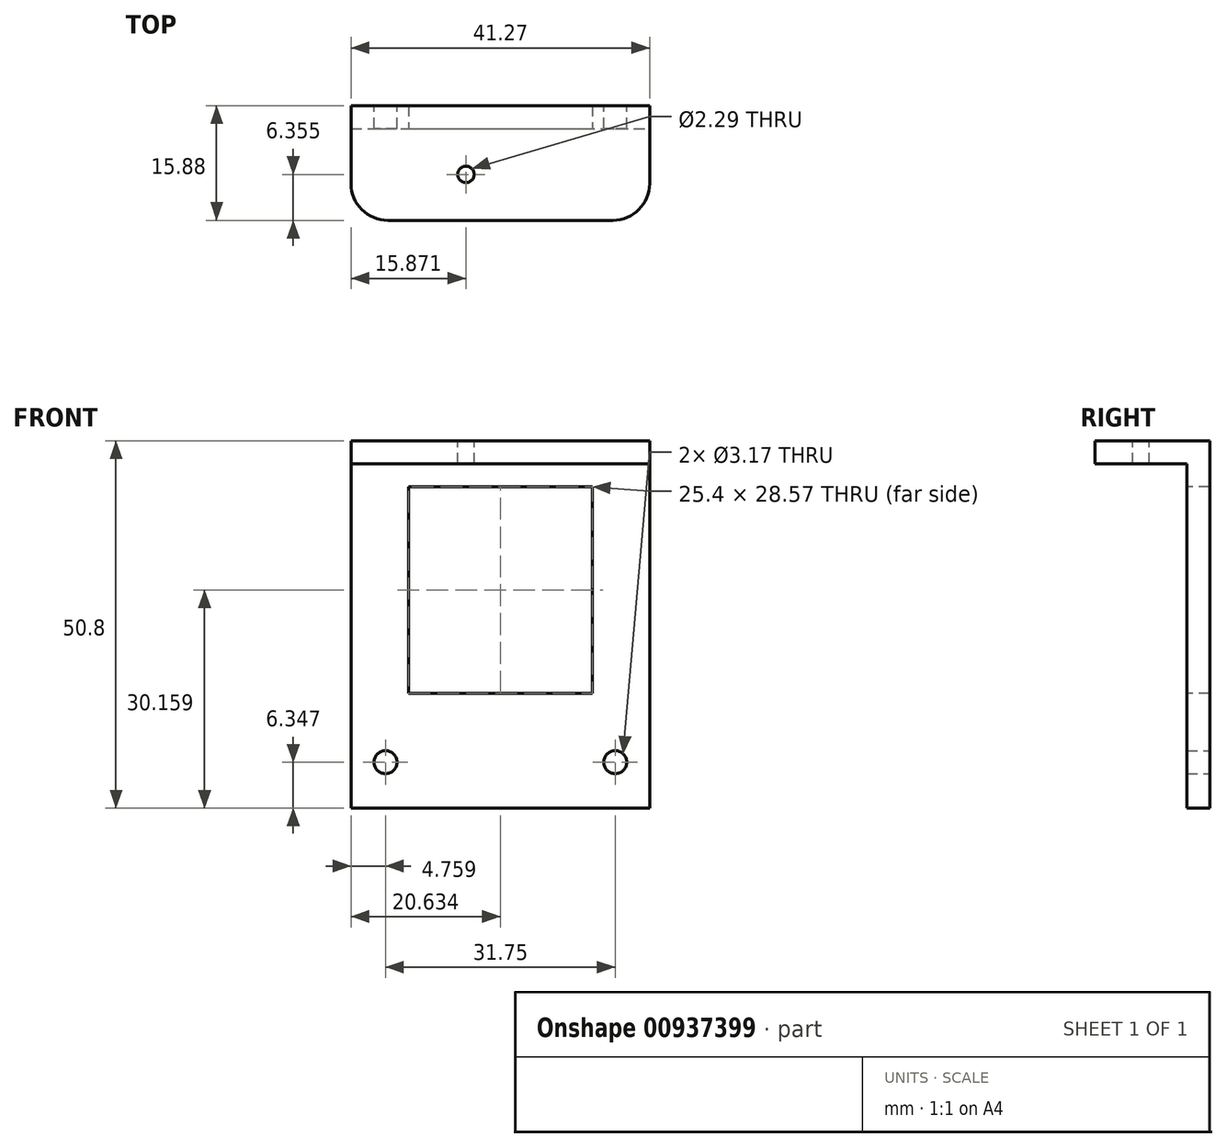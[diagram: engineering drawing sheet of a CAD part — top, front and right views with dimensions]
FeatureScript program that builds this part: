
annotation { "Feature Type Name" : "Feature", "Feature Type Description" : "" }
export const myFeature = defineFeature(function(context is Context, id is Id, definition is map)
    precondition{}
    {
        {
            var Q0;
            Q0=qCreatedBy(makeId("Front.planeOp"),FACE);
            var sketch = newSketch(context, id + "F0", { "sketchPlane" : qUnion([Q0])});
            skLineSegment(sketch, "E0.bottom", {"start": v(18.9, -13.03) * mm, "end": v(-22.38, -13.03) * mm});
            skLineSegment(sketch, "E0.top", {"start": v(18.9, 37.77) * mm, "end": v(-22.38, 37.77) * mm});
            skLineSegment(sketch, "E0.left", {"start": v(18.9, -13.03) * mm, "end": v(18.9, 37.77) * mm});
            skLineSegment(sketch, "E0.right", {"start": v(-22.38, -13.03) * mm, "end": v(-22.38, 37.77) * mm});
            skCircle(sketch, "E1", {"center": v(-17.62, -6.68) * mm, "radius": 1.59 * mm});
            skCircle(sketch, "E2", {"center": v(14.13, -6.68) * mm, "radius": 1.59 * mm});
            skSolve(sketch);
        }
        {
            var Q0;
            Q0 = qSketchRegion(id + "F0", true);
            var Q1;
            Q1=makeQuery(id+"F0.imprint","IMPRINT",FACE,{"disambiguationData":[TD([[makeQuery(id+"F0.imprint","IMPRINT",EDGE,{"derivedFrom":sQuery(id+"F0.wireOp",EDGE,"E0.bottom")}),-1.0]])]});
            extrude(context, id + "F1", {"entities" : qUnion([Q0, Q1]), "depth" : 3.17 * mm, "offsetDistance" : 25.4 * mm});
        }
        {
            var Q0;
            Q0=makeQuery(id+"F1.opExtrude","CAP_FACE",FACE,{"disambiguationData":[OSD([sQuery(id+"F0.wireOp",EDGE,"E0.bottom"),sQuery(id+"F0.wireOp",EDGE,"E0.top"),sQuery(id+"F0.wireOp",EDGE,"E0.left"),sQuery(id+"F0.wireOp",EDGE,"E0.right"),sQuery(id+"F0.wireOp",EDGE,"E1"),sQuery(id+"F0.wireOp",EDGE,"E2")])],"isStart":false});
            var sketch = newSketch(context, id + "F2", { "sketchPlane" : qUnion([Q0])});
            skLineSegment(sketch, "E3.bottom", {"start": v(-22.38, 37.77) * mm, "end": v(18.9, 37.77) * mm});
            skLineSegment(sketch, "E3.top", {"start": v(-22.38, 34.6) * mm, "end": v(18.9, 34.6) * mm});
            skLineSegment(sketch, "E3.left", {"start": v(-22.38, 37.77) * mm, "end": v(-22.38, 34.6) * mm});
            skLineSegment(sketch, "E3.right", {"start": v(18.9, 37.77) * mm, "end": v(18.9, 34.6) * mm});
            skSolve(sketch);
        }
        {
            var Q0;
            Q0 = qSketchRegion(id + "F2", true);
            var Q1;
            Q1=makeQuery(id+"F2.imprint","IMPRINT",FACE,{"disambiguationData":[TD([[makeQuery(id+"F2.imprint","IMPRINT",EDGE,{"derivedFrom":sQuery(id+"F2.wireOp",EDGE,"E3.bottom")}),1.0]])]});
            extrude(context, id + "F3", {"entities" : qUnion([Q0, Q1]), "operationType" : NewBodyOperationType.ADD, "depth" : 12.7 * mm, "offsetDistance" : 25.4 * mm});
        }
        {
            var Q0;
            Q0=makeQuery(id+"F3.boolean.opBoolean","MERGE",FACE,{"derivedFrom":[makeQuery(id+"F1.opExtrude","SWEPT_FACE",FACE,{"disambiguationData":[OSD([sQuery(id+"F0.wireOp",EDGE,"E0.top")])]}),makeQuery(id+"F3.opExtrude","SWEPT_FACE",FACE,{"disambiguationData":[OSD([sQuery(id+"F2.wireOp",EDGE,"E3.bottom")])]})]});
            var sketch = newSketch(context, id + "F4", { "sketchPlane" : qUnion([Q0])});
            skCircle(sketch, "E4", {"center": v(-6.5, -9.52) * mm, "radius": 1.14 * mm});
            skSolve(sketch);
        }
        {
            var Q0;
            Q0=makeQuery(id+"F1.opExtrude","CAP_FACE",FACE,{"disambiguationData":[OSD([sQuery(id+"F0.wireOp",EDGE,"E0.bottom"),sQuery(id+"F0.wireOp",EDGE,"E0.top"),sQuery(id+"F0.wireOp",EDGE,"E0.left"),sQuery(id+"F0.wireOp",EDGE,"E0.right"),sQuery(id+"F0.wireOp",EDGE,"E1"),sQuery(id+"F0.wireOp",EDGE,"E2")])],"isStart":false});
            var sketch = newSketch(context, id + "F5", { "sketchPlane" : qUnion([Q0])});
            skLineSegment(sketch, "E5.bottom", {"start": v(-14.45, 2.84) * mm, "end": v(10.95, 2.84) * mm});
            skLineSegment(sketch, "E5.top", {"start": v(-14.45, 31.42) * mm, "end": v(10.95, 31.42) * mm});
            skLineSegment(sketch, "E5.left", {"start": v(-14.45, 2.84) * mm, "end": v(-14.45, 31.42) * mm});
            skLineSegment(sketch, "E5.right", {"start": v(10.95, 2.84) * mm, "end": v(10.95, 31.42) * mm});
            skSolve(sketch);
        }
        {
            var Q0;
            Q0=makeQuery(id+"F5.imprint","IMPRINT",FACE,{"disambiguationData":[TD([[makeQuery(id+"F5.imprint","IMPRINT",EDGE,{"derivedFrom":sQuery(id+"F5.wireOp",EDGE,"E5.bottom")}),1.0]])]});
            extrude(context, id + "F6", {"entities" : qUnion([Q0]), "operationType" : NewBodyOperationType.REMOVE, "oppositeDirection" : true, "depth" : 3.17 * mm, "offsetDistance" : 25.4 * mm});
        }
        {
            var Q0;
            Q0=makeQuery(id+"F4.imprint","IMPRINT",FACE,{"disambiguationData":[TD([[makeQuery(id+"F4.imprint","IMPRINT",EDGE,{"derivedFrom":sQuery(id+"F4.wireOp",EDGE,"E4")}),1.0]])]});
            extrude(context, id + "F7", {"entities" : qUnion([Q0]), "operationType" : NewBodyOperationType.REMOVE, "oppositeDirection" : true, "depth" : 25.4 * mm, "offsetDistance" : 25.4 * mm});
        }
        {
            var Q0;
            Q0=makeQuery(id+"F3.opExtrude","CAP_EDGE",EDGE,{"disambiguationData":[OSD([sQuery(id+"F2.wireOp",EDGE,"E3.left")])],"isStart":false});
            fillet(context, id + "F8", {"entities" : qUnion([Q0]), "radius" : 5.08 * mm, "tangentPropagation" : true, "allowEdgeOverflow" : false});
        }
        {
            var Q0;
            Q0=makeQuery(id+"F3.opExtrude","CAP_EDGE",EDGE,{"disambiguationData":[OSD([sQuery(id+"F2.wireOp",EDGE,"E3.right")])],"isStart":false});
            fillet(context, id + "F9", {"entities" : qUnion([Q0]), "radius" : 5.08 * mm, "tangentPropagation" : true, "allowEdgeOverflow" : false});
        }
    });
